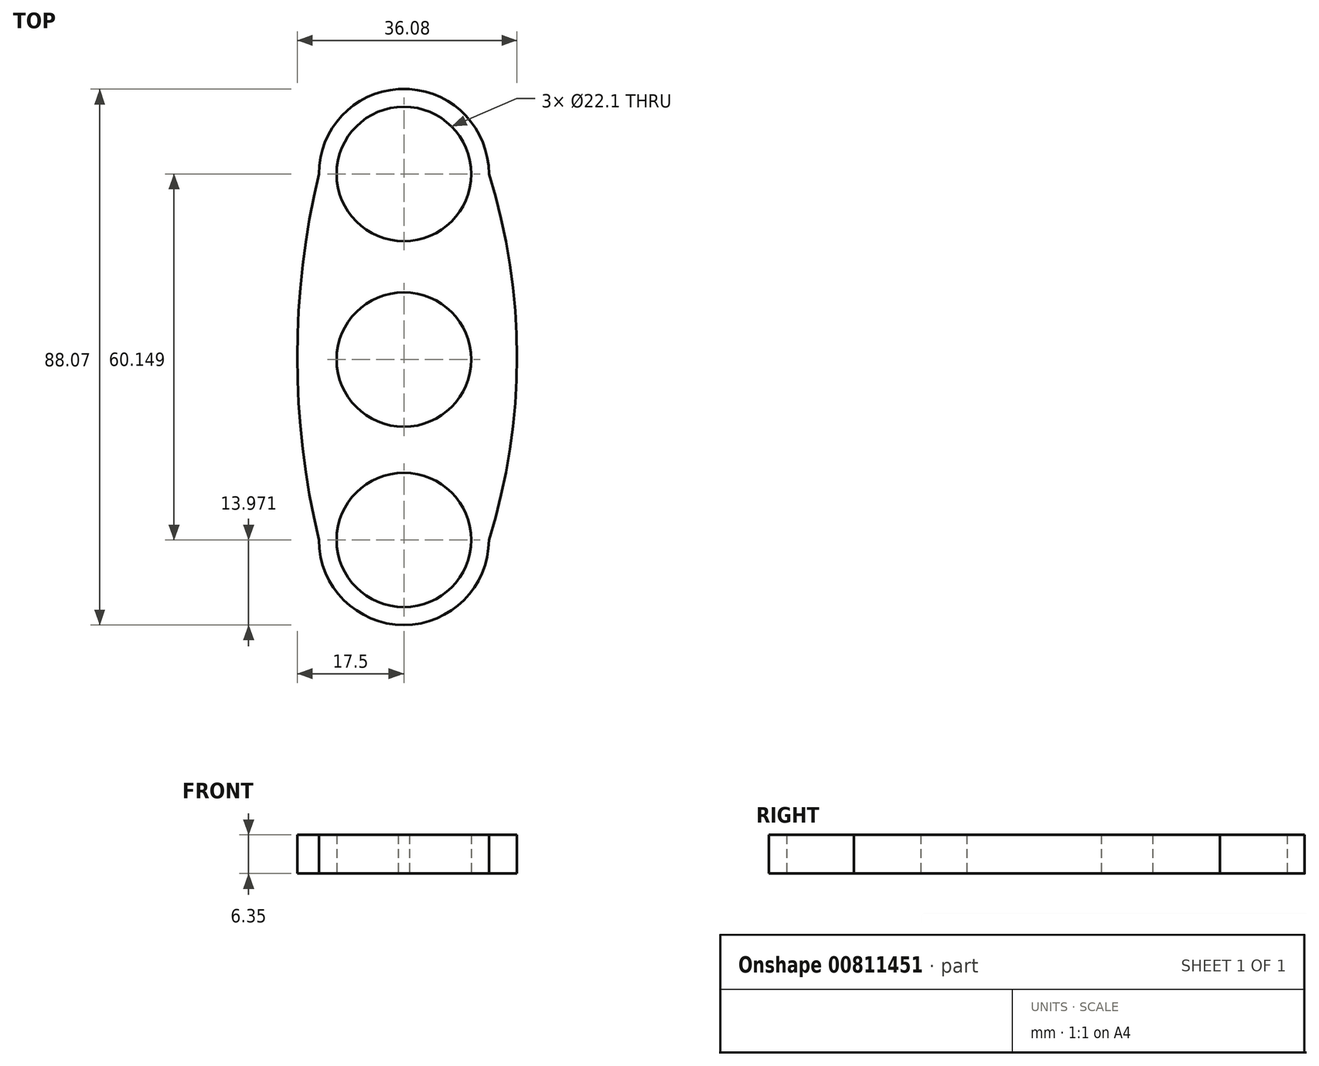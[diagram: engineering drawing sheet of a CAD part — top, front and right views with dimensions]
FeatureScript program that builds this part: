
annotation { "Feature Type Name" : "Feature", "Feature Type Description" : "" }
export const myFeature = defineFeature(function(context is Context, id is Id, definition is map)
    precondition{}
    {
        {
            var Q0;
            Q0=qCreatedBy(makeId("Top.planeOp"),FACE);
            var sketch = newSketch(context, id + "F0", { "sketchPlane" : qUnion([Q0])});
            skCircle(sketch, "E0", {"center": v(0, 0) * mm, "radius": 44.45 * mm});
            skCircle(sketch, "E1", {"center": v(0, 0) * mm, "radius": 13.97 * mm});
            skCircle(sketch, "E2", {"center": v(0, 0) * mm, "radius": 11.05 * mm});
            skCircle(sketch, "E3", {"center": v(0, 30.5) * mm, "radius": 13.97 * mm});
            skCircle(sketch, "E4", {"center": v(0, 30.5) * mm, "radius": 11.05 * mm});
            skCircle(sketch, "E5", {"center": v(0, -29.65) * mm, "radius": 13.97 * mm});
            skCircle(sketch, "E6", {"center": v(0, -29.65) * mm, "radius": 11.05 * mm});
            skArc(sketch, "E7", {"start": v(-13.97, 30.5) * mm, "mid": v(-17.5, 0.43) * mm, "end": v(-13.97, -29.65) * mm});
            skArc(sketch, "E8", {"start": v(13.97, -29.65) * mm, "mid": v(18.58, 0.43) * mm, "end": v(13.97, 30.5) * mm});
            skLineSegment(sketch, "E9", {"start": v(0, 16.53) * mm, "end": v(0, 11.05) * mm});
            skLineSegment(sketch, "E10", {"start": v(0, 0) * mm, "end": v(0, -15.68) * mm});
            skSolve(sketch);
        }
        {
            var Q0;
            {var subQ0=sQuery(id+"F0.wireOp",EDGE,"E7");Q0=makeQuery(id+"F0.imprint","IMPRINT",FACE,{"disambiguationData":[TD([[makeQuery(id+"F0.imprint","IMPRINT",EDGE,{"derivedFrom":subQ0}),1.0]])]});}
            var Q1;
            Q1=makeQuery(id+"F0.imprint","IMPRINT",FACE,{"disambiguationData":[TD([[makeQuery(id+"F0.imprint","IMPRINT",EDGE,{"derivedFrom":sQuery(id+"F0.wireOp",EDGE,"E4")}),-1.0]])]});
            var Q2;
            {var subQ0=sQuery(id+"F0.wireOp",EDGE,"E8");Q2=makeQuery(id+"F0.imprint","IMPRINT",FACE,{"disambiguationData":[TD([[makeQuery(id+"F0.imprint","IMPRINT",EDGE,{"derivedFrom":subQ0}),1.0]])]});}
            var Q3;
            {var subQ0=sQuery(id+"F0.wireOp",EDGE,"E9");var subQ1=sQuery(id+"F0.wireOp",EDGE,"E1");var subQ2=makeQuery(id+"F0.imprint","INTERSECT",VERTEX,{"derivedFrom":[subQ1,subQ0]});Q3=makeQuery(id+"F0.imprint","IMPRINT",FACE,{"disambiguationData":[TD([[makeQuery(id+"F0.imprint","IMPRINT",EDGE,{"disambiguationData":[TD([[subQ2,1.0]])],"derivedFrom":subQ1}),1.0]])]});}
            var Q4;
            {var subQ0=sQuery(id+"F0.wireOp",EDGE,"E9");var subQ1=sQuery(id+"F0.wireOp",EDGE,"E1");var subQ2=makeQuery(id+"F0.imprint","INTERSECT",VERTEX,{"derivedFrom":[subQ1,subQ0]});Q4=makeQuery(id+"F0.imprint","IMPRINT",FACE,{"disambiguationData":[TD([[makeQuery(id+"F0.imprint","IMPRINT",EDGE,{"disambiguationData":[TD([[subQ2,-1.0]])],"derivedFrom":subQ1}),1.0]])]});}
            var Q5;
            Q5=makeQuery(id+"F0.imprint","IMPRINT",FACE,{"disambiguationData":[TD([[makeQuery(id+"F0.imprint","IMPRINT",EDGE,{"derivedFrom":sQuery(id+"F0.wireOp",EDGE,"E6")}),-1.0]])]});
            extrude(context, id + "F1", {"entities" : qUnion([Q0, Q1, Q2, Q3, Q4, Q5]), "depth" : 6.35 * mm, "offsetDistance" : 25.4 * mm});
        }
    });
